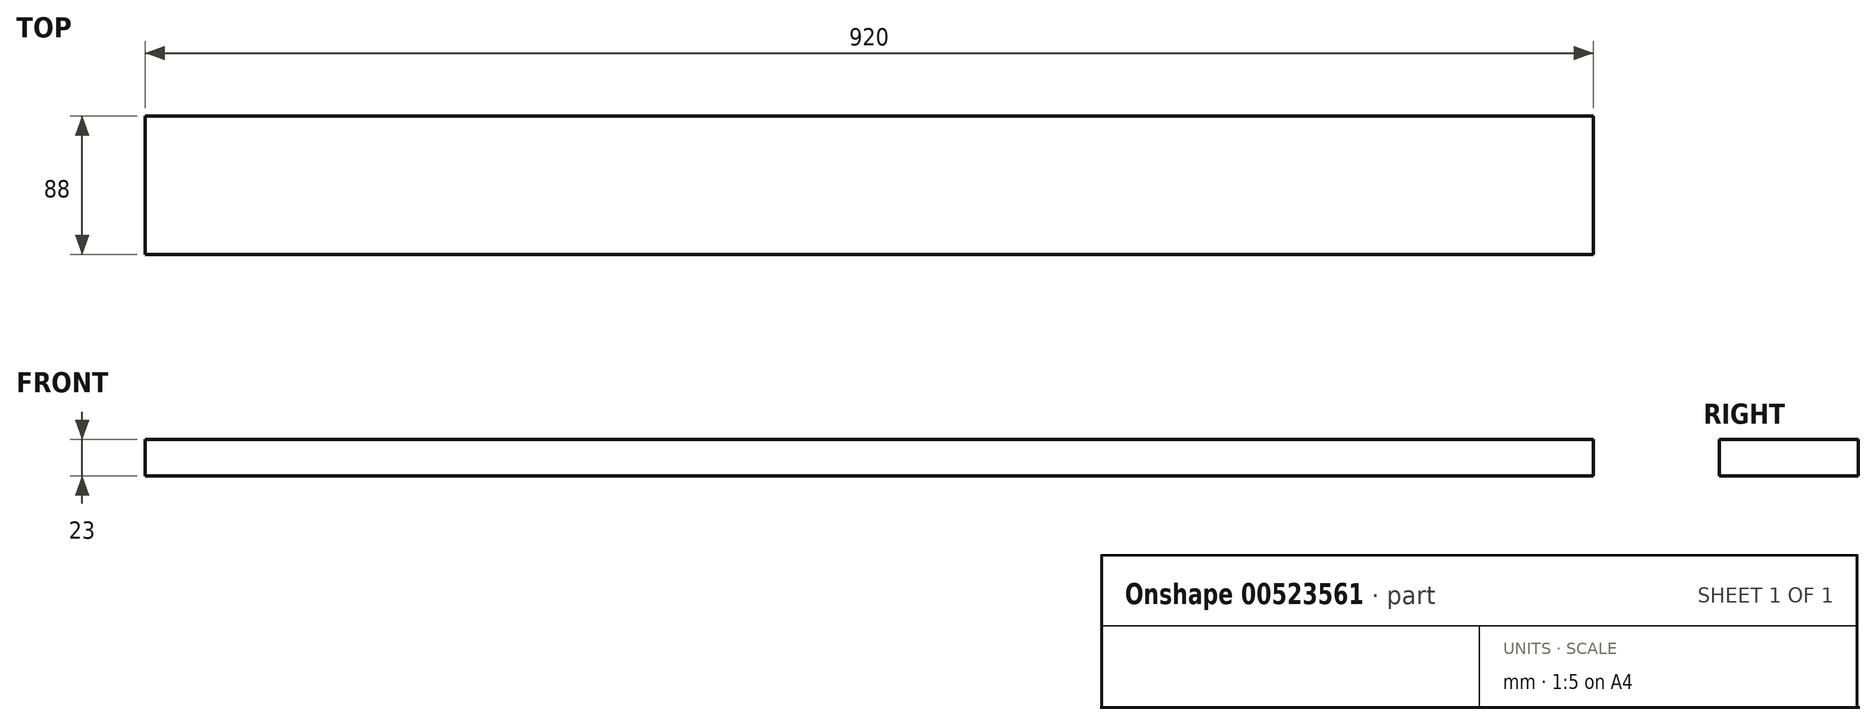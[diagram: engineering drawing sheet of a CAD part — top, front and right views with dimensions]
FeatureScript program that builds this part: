
annotation { "Feature Type Name" : "Feature", "Feature Type Description" : "" }
export const myFeature = defineFeature(function(context is Context, id is Id, definition is map)
    precondition{}
    {
        {
            var Q0;
            Q0=qCreatedBy(makeId("Top.planeOp"),FACE);
            var sketch = newSketch(context, id + "F0", { "sketchPlane" : qUnion([Q0])});
            skLineSegment(sketch, "E0.bottom", {"start": v(460, -44) * mm, "end": v(-460, -44) * mm});
            skLineSegment(sketch, "E0.top", {"start": v(460, 44) * mm, "end": v(-460, 44) * mm});
            skLineSegment(sketch, "E0.left", {"start": v(460, -44) * mm, "end": v(460, 44) * mm});
            skLineSegment(sketch, "E0.right", {"start": v(-460, -44) * mm, "end": v(-460, 44) * mm});
            skPoint(sketch, "E0.middle", {"position": v(0, 0) * mm});
            skSolve(sketch);
        }
        {
            var Q0;
            Q0 = qSketchRegion(id + "F0", true);
            var Q1;
            Q1=makeQuery(id+"F0.imprint","IMPRINT",FACE,{"disambiguationData":[TD([[makeQuery(id+"F0.imprint","IMPRINT",EDGE,{"derivedFrom":sQuery(id+"F0.wireOp",EDGE,"E0.bottom")}),-1.0]])]});
            extrude(context, id + "F1", {"entities" : qUnion([Q0, Q1]), "depth" : 23 * mm, "offsetDistance" : 25 * mm});
        }
    });
